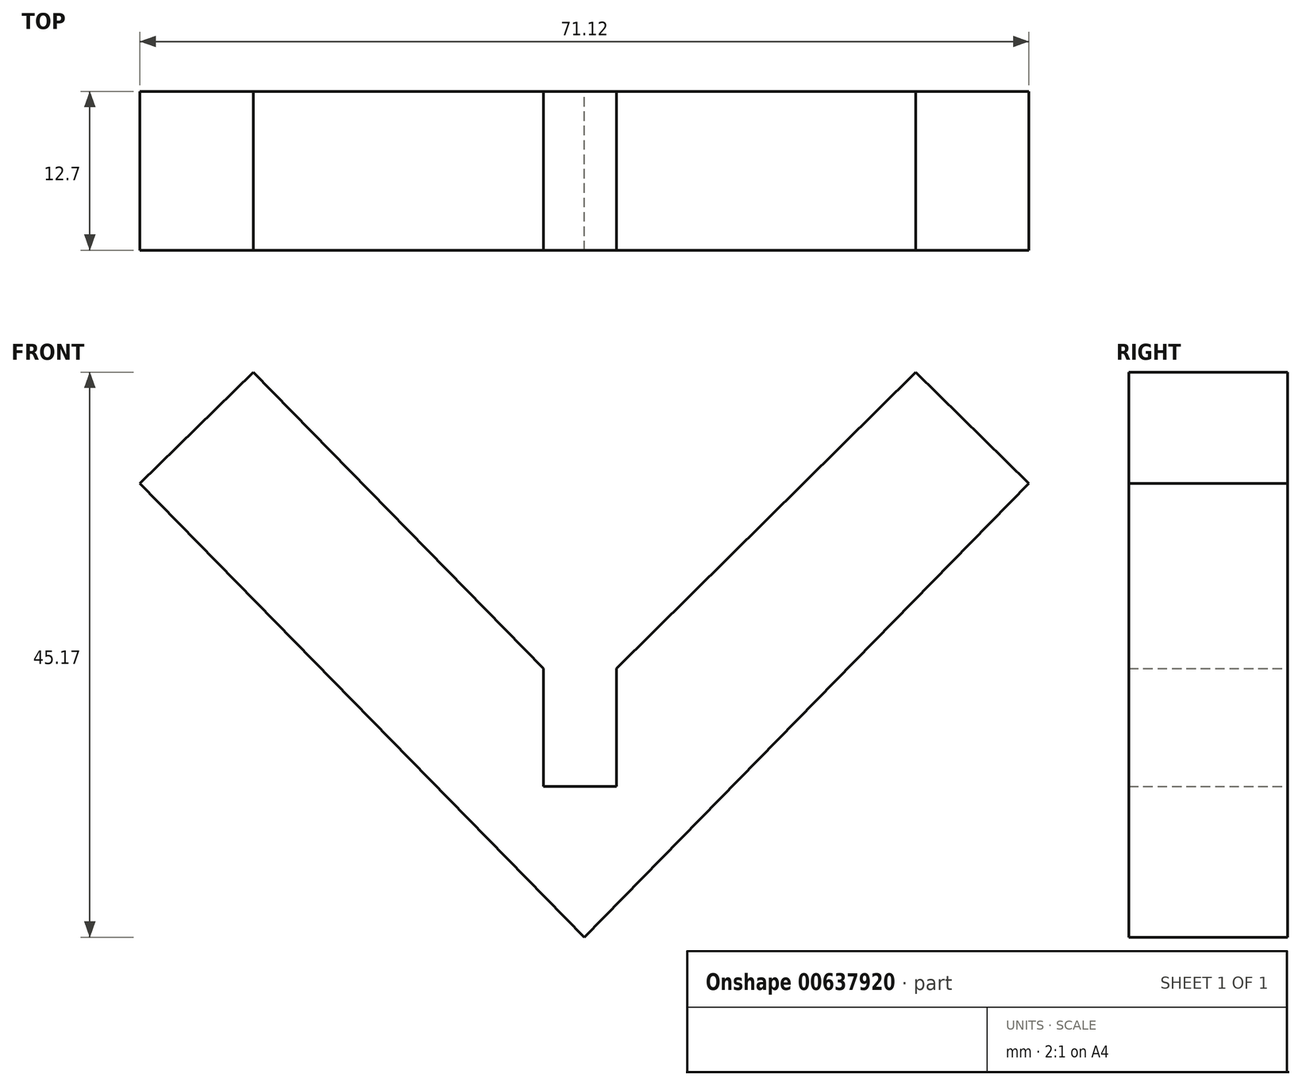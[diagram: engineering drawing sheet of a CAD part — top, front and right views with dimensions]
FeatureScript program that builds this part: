
annotation { "Feature Type Name" : "Feature", "Feature Type Description" : "" }
export const myFeature = defineFeature(function(context is Context, id is Id, definition is map)
    precondition{}
    {
        {
            var Q0;
            Q0=qCreatedBy(makeId("Front.planeOp"),FACE);
            var sketch = newSketch(context, id + "F0", { "sketchPlane" : qUnion([Q0])});
            skLineSegment(sketch, "E0", {"start": v(-35.56, 36.28) * mm, "end": v(0, 0) * mm});
            skLineSegment(sketch, "E1", {"start": v(0, 0) * mm, "end": v(35.56, 36.28) * mm});
            skLineSegment(sketch, "E2", {"start": v(-35.56, 36.28) * mm, "end": v(-26.5, 45.17) * mm});
            skLineSegment(sketch, "E3", {"start": v(-26.5, 45.17) * mm, "end": v(-3.28, 21.49) * mm});
            skLineSegment(sketch, "E4", {"start": v(-3.28, 21.49) * mm, "end": v(-3.28, 3.34) * mm});
            skLineSegment(sketch, "E5", {"start": v(35.56, 36.28) * mm, "end": v(26.5, 45.17) * mm});
            skLineSegment(sketch, "E6", {"start": v(26.5, 45.17) * mm, "end": v(2.55, 21.49) * mm});
            skLineSegment(sketch, "E7", {"start": v(2.55, 21.49) * mm, "end": v(2.55, 2.6) * mm});
            skLineSegment(sketch, "E8", {"start": v(2.55, 12.04) * mm, "end": v(-3.28, 12.04) * mm});
            skSolve(sketch);
        }
        {
            var Q0;
            Q0 = qSketchRegion(id + "F0", true);
            extrude(context, id + "F1", {"entities" : qUnion([Q0]), "depth" : 12.7 * mm, "offsetDistance" : 25.4 * mm});
        }
    });
